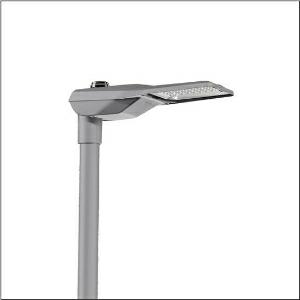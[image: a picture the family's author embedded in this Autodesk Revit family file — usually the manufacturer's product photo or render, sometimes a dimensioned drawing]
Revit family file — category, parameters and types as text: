
# Revit family: streetlight_sl_21_mini___stw1_0a_5xe6e37n08jb_6c36
name_source: partatom
category: Lighting Fixtures
units: mm (PartAtom-declared; Revit-internal decimal feet)

## family parameters
Cut with Voids When Loaded = No
Host = Face
Light Source = No
Part Type = Normal
Room Calculation Point = No
Round Connector Dimension = Use Diameter
Shared = No

## types (1)
- --- (1 x LED, 12830 lm, 87.3 W, 3000K)
    Apparent Load = 87 VA
    CIE Flux Codes = 39 75 98 100 100
    Color Rendering = 70
    Color Temperature = 3000K
    Default Elevation = 1800 mm
    Description = Streetlight SL 21 mini, mast luminaire, primary light control with lens, of PMMA, primary optical cover: cover, of toughened safety glass, transparent, light distribution: STW1.0a, light emission: direct distribution, primary light characteristic: asymmetric, installation type: side-entry, LED, 3G 2.5mm², High Power LED, rated luminous flux: 12.830lm, luminous efficacy: 147lm/W, light colour: 730, colour temperature: 3000K, control gear: NEMA (7pin), control: overheat protection, pre-setting: linear dimming characteristic, constant luminous flux control, time-dependent luminous flux control, flexible luminous flux parameterisation, mains connection: 230..240V, AC, 50/60Hz, connection cable pre-assembled, cable length: 10,5m, wiring characteristics: H05VV-F, start of lifetime: 87W, end of service life: 90W, reduction: 40W, luminaire housing, of diecast aluminium (EN AC-44300), powder-coated, Siteco® metallic grey (DB 702S), corrosivity category C5 mid according to DIN EN ISO 12944, multi-level sealing system, sealing non-destructively replaceable, inclination adjustable: 0°, 5°, 10°, 15°, length: 628mm, width: 235mm, height: 110mm, spigot size: 42mm (side-entry), mounting height: 4..8m, protection rating (complete): IP66, insulation class (complete): insulation class I (protective earthing), certification: CE, ENEC, ENEC+, VDE, impact resistance: IK10, permissible operating ambient temperature for outdoor applications: -40..+50°C, standard-compliant lighting for roads and squares, packaging unit: 1 piece

Light Distribution: STW1.0a
    Height = 110 mm
    Lamp = 1 x LED
    Lamp Light Flux = 12830 lm
    Lamp Power = 87.3 W
    Lamp count = 1
    Length = 625 mm
    Luminous efficacy = 147 lm/W
    Manufacturer = Siteco
    ModVariant = No
    Model = 5XE6E37N08JB
    Number of Poles = 1
    OnlyDefault = Yes
    Power Factor = 1
    Product Name = Streetlight SL 21 mini | STW1.0a
    Product group = mast luminaire | pylon top
    ProductGroupID = 6100
    Protection Class = Protection class I
    Protection Degree = IP 66
    RLX_Detail_Level = 1
    RLX_Emergency_Light_Flux = 0 lm
    RLX_Emergency_Type = 0
    RLX_Emergency_Type_DB = No
    RlxData = <blob elided: 26077 chars, md5=88b70d5e>
    Socket = socket
    Standby Power = 0 W
    System Light Flux = 12830 lm
    System Power = 87 W
    Type Comments = factory setting: luminous flux: 100 % | dim-lin: 254 | 915 mA
    Type Image = l_1294379.jpg
    URL = http://relux.com
    VarID = @adj_156491
    Voltage = 0 V
    Weight = 0.00 kg
    Width = 234 mm

## geometry (parser evidence)
native form markers: Blend x4, Sweep x11
no freeform markers — native parametric forms only
